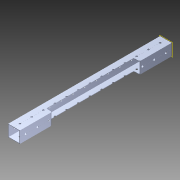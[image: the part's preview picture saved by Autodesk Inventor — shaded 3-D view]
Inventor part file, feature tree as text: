
AUTODESK INVENTOR PART (.ipt)
format: ipt  version: 2014 (Build 180170000, 170)  size: 1,248,768 bytes
history: native  units: in
note: dims shown in document units (in); Inventor stores cm internally (conversion verified against a paired STEP export)
features: extrude x2, sketch x2, pattern_circular x1, other x1, plane x1, imported_body x1
ambient origin geometry x8: Origin, YZ Plane, XZ Plane, XY Plane, X Axis, Y Axis, Z Axis, Center Point
bodies: Body1 (feature_tree)
feature tree (8):
  pattern_circular  "CirPattern2"
  other  "217-3426-STEP1"
  plane  "Work Plane1"
  extrude  "Extrusion1"  Depth=3937.0079in TaperAngle=0.0deg
  extrude  "Extrusion3"  Depth=0.125in
  imported_body  "Base1"
  sketch  "Sketch1"  dims[d0=-13.0in d1=3937.0079in d2=0.0in]
  sketch  "Sketch4"  dims[d6=7.5in d9=0.125in d10=0.125in d11=0.5in d12=2.75in d13=3.937in d14=0.0in]
